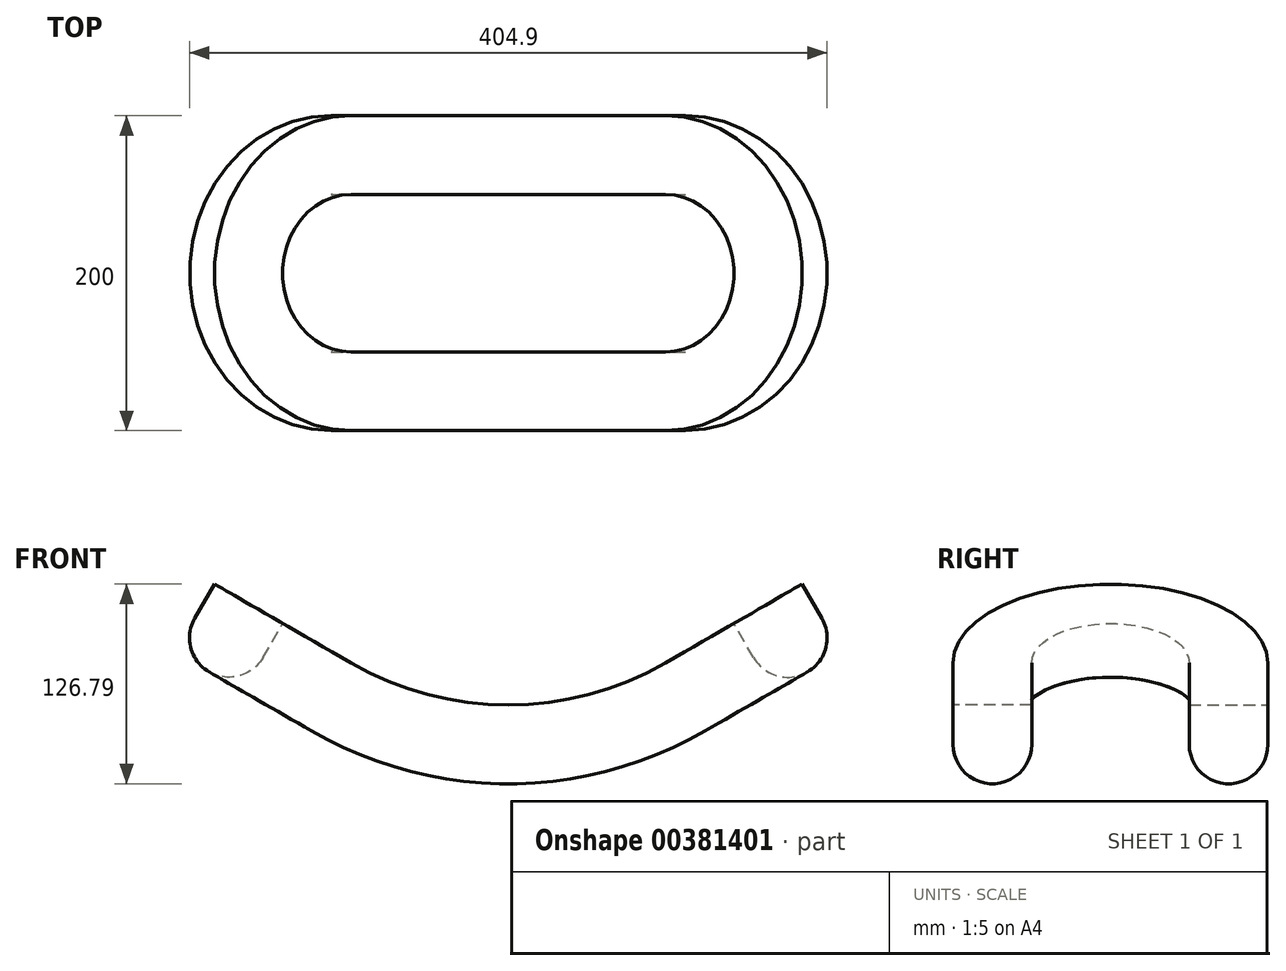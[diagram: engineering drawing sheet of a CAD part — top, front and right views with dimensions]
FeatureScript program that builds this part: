
annotation { "Feature Type Name" : "Feature", "Feature Type Description" : "" }
export const myFeature = defineFeature(function(context is Context, id is Id, definition is map)
    precondition{}
    {
        {
            var Q0;
            Q0=qCreatedBy(makeId("Front.planeOp"),FACE);
            var sketch = newSketch(context, id + "F0", { "sketchPlane" : qUnion([Q0])});
            skArc(sketch, "E0", {"start": v(0, 0) * mm, "mid": v(51.76, 6.81) * mm, "end": v(100, 26.8) * mm});
            skLineSegment(sketch, "E1", {"start": v(100, 26.8) * mm, "end": v(186.6, 76.8) * mm});
            skLineSegment(sketch, "E2", {"start": v(0, 0) * mm, "end": v(0, 200) * mm, "construction": true});
            skLineSegment(sketch, "E3", {"start": v(0, 200) * mm, "end": v(100, 26.8) * mm, "construction": true});
            skSolve(sketch);
        }
        {
            var Q0;
            Q0=sQuery(id+"F0.wireOp",EDGE,"E1");
            var Q1;
            Q1=sQuery(id+"F0.wireOp",EDGE,"E0");
            extrude(context, id + "F1", {"bodyType" : ToolBodyType.SURFACE, "operationType" : NewBodyOperationType.INTERSECT, "surfaceEntities" : qUnion([Q0, Q1]), "depth" : 100 * mm});
        }
        {
            var Q0;
            Q0=makeQuery(id+"F1.opExtrude","SWEPT_FACE",FACE,{"disambiguationData":[OSD([sQuery(id+"F0.wireOp",EDGE,"E1")])]});
            var sketch = newSketch(context, id + "F2", { "sketchPlane" : qUnion([Q0])});
            skArc(sketch, "E4", {"start": v(200, 0) * mm, "mid": v(170.71, 70.71) * mm, "end": v(100, 100) * mm});
            skSolve(sketch);
        }
        {
            var Q0;
            Q0=qCreatedBy(makeId("Right.planeOp"),FACE);
            var sketch = newSketch(context, id + "F3", { "sketchPlane" : qUnion([Q0])});
            skLineSegment(sketch, "E5.bottom", {"start": v(-100, 0) * mm, "end": v(-50, 0) * mm});
            skLineSegment(sketch, "E5.top", {"start": v(-100, -25) * mm, "end": v(-50, -25) * mm, "construction": true});
            skLineSegment(sketch, "E5.left", {"start": v(-100, 0) * mm, "end": v(-100, -25) * mm});
            skLineSegment(sketch, "E5.right", {"start": v(-50, 0) * mm, "end": v(-50, -25) * mm});
            skArc(sketch, "E6", {"start": v(-100, -25) * mm, "mid": v(-75, -50) * mm, "end": v(-50, -25) * mm});
            skSolve(sketch);
        }
        {
            var Q0;
            Q0=makeQuery(id+"F3.imprint","IMPRINT",FACE,{"disambiguationData":[TD([[makeQuery(id+"F3.imprint","IMPRINT",EDGE,{"derivedFrom":sQuery(id+"F3.wireOp",EDGE,"E5.bottom")}),-1.0]])]});
            var Q1;
            Q1=makeQuery(id+"F1.opExtrude","CAP_EDGE",EDGE,{"disambiguationData":[OSD([sQuery(id+"F0.wireOp",EDGE,"E0")])],"isStart":false});
            var Q2;
            Q2=sQuery(id+"F2.wireOp",EDGE,"E4");
            sweep(context, id + "F4", {"profiles" : qUnion([Q0]), "path" : qUnion([Q1, Q2])});
        }
        {
            var Q0;
            Q0=makeQuery(id+"F4.opSweep","SWEPT_BODY",BODY,{"disambiguationData":[OSD([sQuery(id+"F2.wireOp",EDGE,"E4"),sQuery(id+"F3.wireOp",EDGE,"E5.bottom"),sQuery(id+"F3.wireOp",EDGE,"E5.left"),sQuery(id+"F3.wireOp",EDGE,"E5.right"),sQuery(id+"F3.wireOp",EDGE,"E6")])]});
            var Q1;
            Q1=qCreatedBy(makeId("Front.planeOp"),FACE);
            mirror(context, id + "F5", {"operationType" : NewBodyOperationType.ADD, "entities" : qUnion([Q0]), "mirrorPlane" : qUnion([Q1])});
        }
        {
            var Q0;
            Q0=makeQuery(id+"F4.opSweep","SWEPT_BODY",BODY,{"disambiguationData":[OSD([sQuery(id+"F2.wireOp",EDGE,"E4"),sQuery(id+"F3.wireOp",EDGE,"E5.bottom"),sQuery(id+"F3.wireOp",EDGE,"E5.left"),sQuery(id+"F3.wireOp",EDGE,"E5.right"),sQuery(id+"F3.wireOp",EDGE,"E6")])]});
            var Q1;
            Q1=qCreatedBy(makeId("Right.planeOp"),FACE);
            mirror(context, id + "F6", {"operationType" : NewBodyOperationType.ADD, "entities" : qUnion([Q0]), "mirrorPlane" : qUnion([Q1])});
        }
    });
